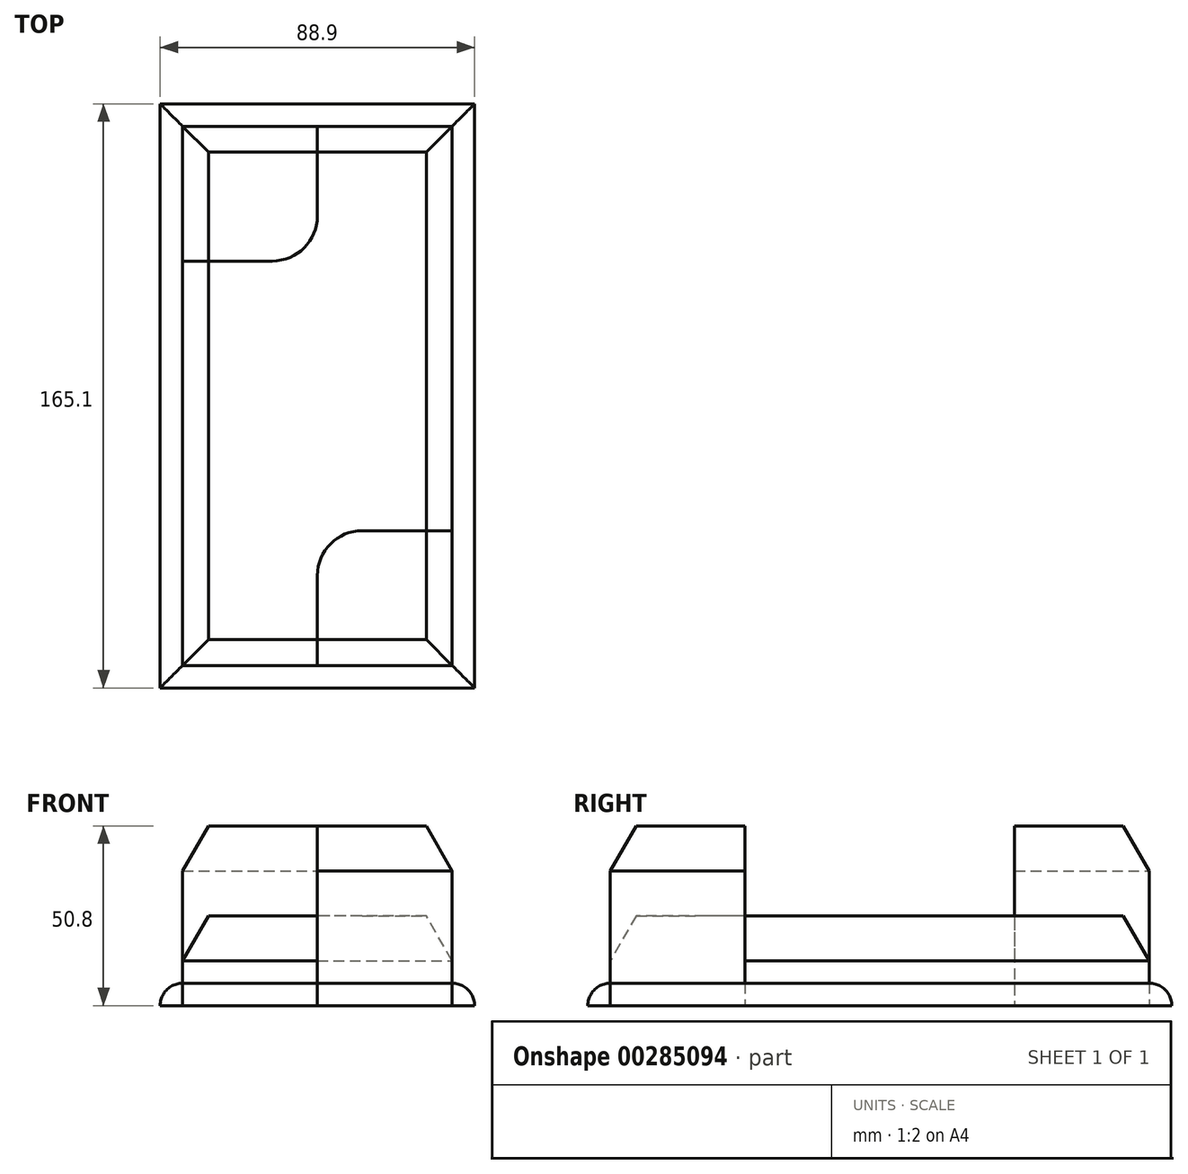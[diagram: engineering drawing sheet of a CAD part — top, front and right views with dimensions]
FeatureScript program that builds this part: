
annotation { "Feature Type Name" : "Feature", "Feature Type Description" : "" }
export const myFeature = defineFeature(function(context is Context, id is Id, definition is map)
    precondition{}
    {
        {
            var Q0;
            Q0=qCreatedBy(makeId("Top.planeOp"),FACE);
            var sketch = newSketch(context, id + "F0", { "sketchPlane" : qUnion([Q0])});
            skLineSegment(sketch, "E0.bottom", {"start": v(-39.47, -83.35) * mm, "end": v(36.73, -83.35) * mm});
            skLineSegment(sketch, "E0.top", {"start": v(-39.47, 69.05) * mm, "end": v(36.73, 69.05) * mm});
            skLineSegment(sketch, "E0.left", {"start": v(-39.47, -83.35) * mm, "end": v(-39.47, 69.05) * mm});
            skLineSegment(sketch, "E0.right", {"start": v(36.73, -83.35) * mm, "end": v(36.73, 69.05) * mm});
            skLineSegment(sketch, "E1.bottom", {"start": v(-45.82, -89.7) * mm, "end": v(43.08, -89.7) * mm});
            skLineSegment(sketch, "E1.top", {"start": v(-45.82, 75.4) * mm, "end": v(43.08, 75.4) * mm});
            skLineSegment(sketch, "E1.left", {"start": v(-45.82, -89.7) * mm, "end": v(-45.82, 75.4) * mm});
            skLineSegment(sketch, "E1.right", {"start": v(43.08, -89.7) * mm, "end": v(43.08, 75.4) * mm});
            skLineSegment(sketch, "E2", {"start": v(-1.37, 69.05) * mm, "end": v(-1.37, 43.65) * mm});
            skLineSegment(sketch, "E3", {"start": v(-14.07, 30.95) * mm, "end": v(-39.47, 30.95) * mm});
            skPoint(sketch, "E4.visualSharp", {"position": v(-1.37, 30.95) * mm});
            skArc(sketch, "E4.filletArc", {"start": v(-14.07, 30.95) * mm, "mid": v(-5.1, 34.67) * mm, "end": v(-1.37, 43.65) * mm});
            skLineSegment(sketch, "E5", {"start": v(-1.37, -83.35) * mm, "end": v(-1.37, -57.95) * mm});
            skLineSegment(sketch, "E6", {"start": v(11.33, -45.25) * mm, "end": v(36.73, -45.25) * mm});
            skPoint(sketch, "E7.visualSharp", {"position": v(-1.37, -45.25) * mm});
            skArc(sketch, "E7.filletArc", {"start": v(11.33, -45.25) * mm, "mid": v(2.35, -48.97) * mm, "end": v(-1.37, -57.95) * mm});
            skSolve(sketch);
        }
        {
            var Q0;
            Q0 = qSketchRegion(id + "F0", true);
            extrude(context, id + "F1", {"entities" : qUnion([Q0]), "depth" : 6.35 * mm});
        }
        {
            var Q0;
            {var subQ9=sQuery(id+"F0.wireOp",EDGE,"E2");Q0=makeQuery(id+"F0.imprint","IMPRINT",FACE,{"disambiguationData":[TD([[makeQuery(id+"F0.imprint","IMPRINT",EDGE,{"derivedFrom":subQ9}),1.0]])]});}
            extrude(context, id + "F2", {"entities" : qUnion([Q0]), "depth" : 25.4 * mm});
        }
        {
            var Q0;
            {var subQ4=sQuery(id+"F0.wireOp",EDGE,"E2");Q0=makeQuery(id+"F0.imprint","IMPRINT",FACE,{"disambiguationData":[TD([[makeQuery(id+"F0.imprint","IMPRINT",EDGE,{"derivedFrom":subQ4}),-1.0]])]});}
            var Q1;
            {var subQ0=sQuery(id+"F0.wireOp",EDGE,"E5");Q1=makeQuery(id+"F0.imprint","IMPRINT",FACE,{"disambiguationData":[TD([[makeQuery(id+"F0.imprint","IMPRINT",EDGE,{"derivedFrom":subQ0}),-1.0]])]});}
            extrude(context, id + "F3", {"entities" : qUnion([Q0, Q1]), "depth" : 50.8 * mm});
        }
        {
            var Q0;
            Q0=makeQuery(id+"F1.opExtrude","CAP_EDGE",EDGE,{"disambiguationData":[OSD([sQuery(id+"F0.wireOp",EDGE,"E1.bottom")])],"isStart":false});
            var Q1;
            Q1=makeQuery(id+"F1.opExtrude","CAP_EDGE",EDGE,{"disambiguationData":[OSD([sQuery(id+"F0.wireOp",EDGE,"E1.right")])],"isStart":false});
            var Q2;
            Q2=makeQuery(id+"F1.opExtrude","CAP_EDGE",EDGE,{"disambiguationData":[OSD([sQuery(id+"F0.wireOp",EDGE,"E1.left")])],"isStart":false});
            var Q3;
            Q3=makeQuery(id+"F1.opExtrude","CAP_EDGE",EDGE,{"disambiguationData":[OSD([sQuery(id+"F0.wireOp",EDGE,"E1.top")])],"isStart":false});
            fillet(context, id + "F4", {"entities" : qUnion([Q0, Q1, Q2, Q3]), "radius" : 6.35 * mm, "tangentPropagation" : true, "allowEdgeOverflow" : false});
        }
        {
            var Q0;
            Q0=makeQuery(id+"F3.opExtrude","CAP_EDGE",EDGE,{"disambiguationData":[OSD([sQuery(id+"F0.wireOp",EDGE,"E0.bottom")])],"isStart":false});
            var Q1;
            Q1=makeQuery(id+"F3.opExtrude","CAP_EDGE",EDGE,{"disambiguationData":[OSD([sQuery(id+"F0.wireOp",EDGE,"E0.right")])],"isStart":false});
            var Q2;
            Q2=makeQuery(id+"F2.opExtrude","CAP_EDGE",EDGE,{"disambiguationData":[OSD([sQuery(id+"F0.wireOp",EDGE,"E0.right")])],"isStart":false});
            var Q3;
            Q3=makeQuery(id+"F2.opExtrude","CAP_EDGE",EDGE,{"disambiguationData":[OSD([sQuery(id+"F0.wireOp",EDGE,"E0.top")])],"isStart":false});
            var Q4;
            Q4=makeQuery(id+"F2.opExtrude","CAP_EDGE",EDGE,{"disambiguationData":[OSD([sQuery(id+"F0.wireOp",EDGE,"E0.left")])],"isStart":false});
            var Q5;
            Q5=makeQuery(id+"F2.opExtrude","CAP_EDGE",EDGE,{"disambiguationData":[OSD([sQuery(id+"F0.wireOp",EDGE,"E0.bottom")])],"isStart":false});
            chamfer(context, id + "F5", {"entities" : qUnion([Q0, Q1, Q2, Q3, Q4, Q5]), "chamferType" : ChamferType.OFFSET_ANGLE, "width" : 12.7 * mm, "oppositeDirection" : true, "angle" : 30 * degree, "tangentPropagation" : true});
        }
        {
            var Q0;
            Q0=makeQuery(id+"F3.opExtrude","CAP_EDGE",EDGE,{"disambiguationData":[OSD([sQuery(id+"F0.wireOp",EDGE,"E0.top")])],"isStart":false});
            var Q1;
            Q1=makeQuery(id+"F3.opExtrude","CAP_EDGE",EDGE,{"disambiguationData":[OSD([sQuery(id+"F0.wireOp",EDGE,"E0.left")])],"isStart":false});
            chamfer(context, id + "F6", {"entities" : qUnion([Q0, Q1]), "chamferType" : ChamferType.OFFSET_ANGLE, "width" : 12.7 * mm, "oppositeDirection" : false, "angle" : 30 * degree, "tangentPropagation" : true});
        }
    });
